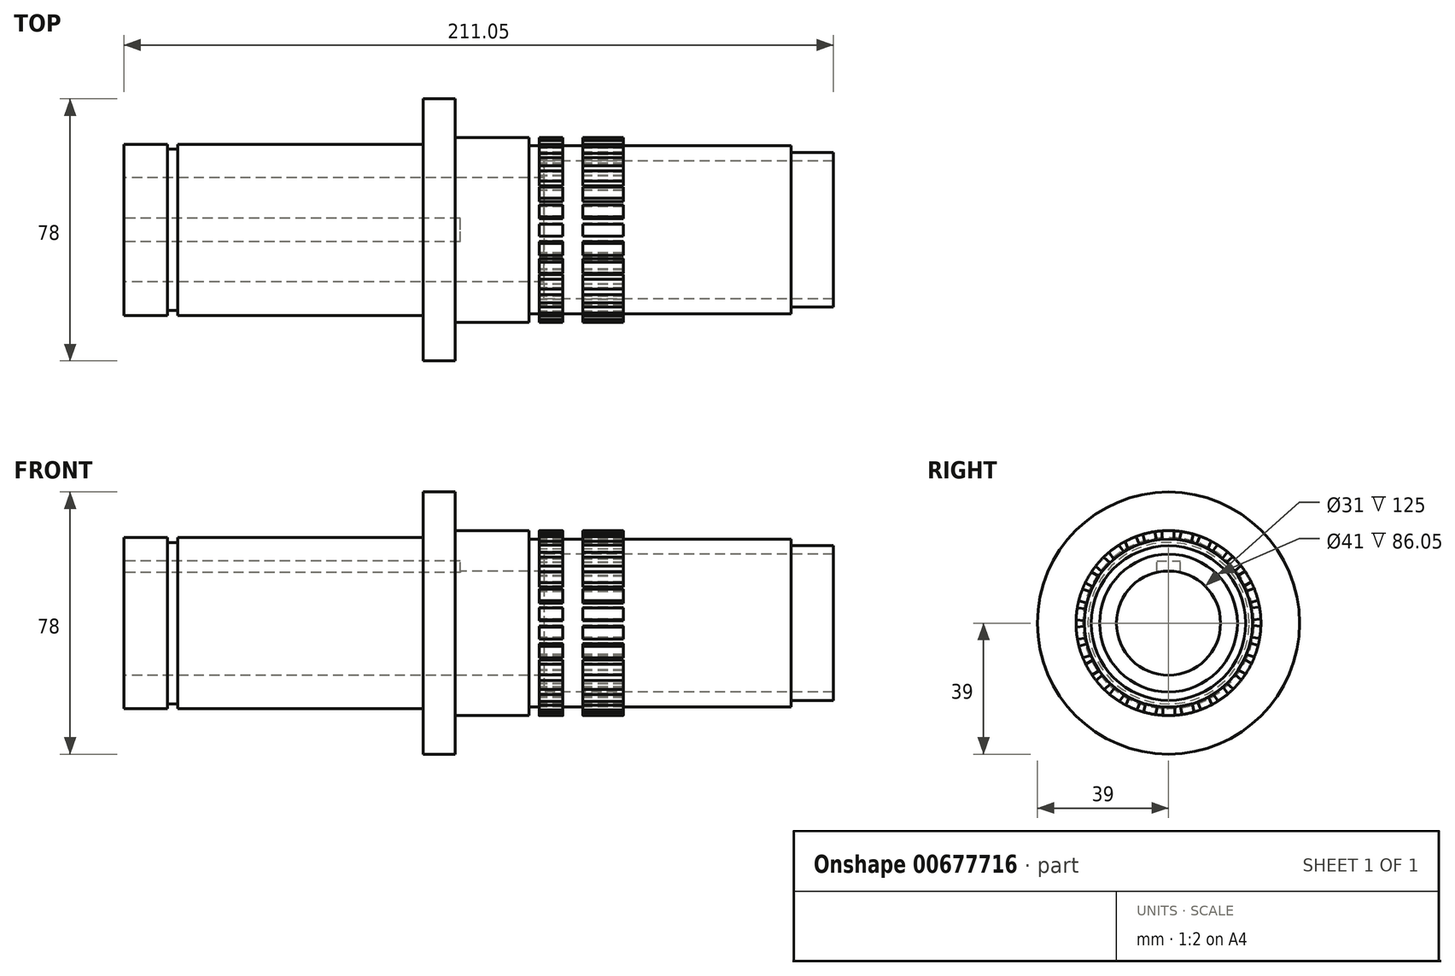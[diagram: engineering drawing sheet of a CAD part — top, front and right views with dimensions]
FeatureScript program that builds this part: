
annotation { "Feature Type Name" : "Feature", "Feature Type Description" : "" }
export const myFeature = defineFeature(function(context is Context, id is Id, definition is map)
    precondition{}
    {
        {
            var Q0;
            Q0=qCreatedBy(makeId("Front.planeOp"),FACE);
            var sketch = newSketch(context, id + "F0", { "sketchPlane" : qUnion([Q0])});
            skLineSegment(sketch, "E0", {"start": v(-135.23, 0) * mm, "end": v(176.63, 0) * mm, "construction": true});
            skLineSegment(sketch, "E1", {"start": v(-98.55, 15.5) * mm, "end": v(26.45, 15.5) * mm});
            skLineSegment(sketch, "E2", {"start": v(26.45, 15.5) * mm, "end": v(26.45, 20.5) * mm});
            skLineSegment(sketch, "E3", {"start": v(26.45, 20.5) * mm, "end": v(112.5, 20.5) * mm});
            skLineSegment(sketch, "E4", {"start": v(112.5, 20.5) * mm, "end": v(112.5, 23) * mm});
            skLineSegment(sketch, "E5", {"start": v(112.5, 23) * mm, "end": v(100, 23) * mm});
            skLineSegment(sketch, "E6", {"start": v(100, 23) * mm, "end": v(100, 25) * mm});
            skLineSegment(sketch, "E7", {"start": v(100, 25) * mm, "end": v(22, 25) * mm});
            skLineSegment(sketch, "E8", {"start": v(22, 25) * mm, "end": v(22, 27.5) * mm});
            skLineSegment(sketch, "E9", {"start": v(22, 27.5) * mm, "end": v(0, 27.5) * mm});
            skLineSegment(sketch, "E10", {"start": v(0, 27.5) * mm, "end": v(0, 39) * mm});
            skLineSegment(sketch, "E11", {"start": v(0, 39) * mm, "end": v(-9.55, 39) * mm});
            skLineSegment(sketch, "E12", {"start": v(-9.55, 39) * mm, "end": v(-9.55, 25.5) * mm});
            skLineSegment(sketch, "E13", {"start": v(-9.55, 25.5) * mm, "end": v(-82.55, 25.5) * mm});
            skLineSegment(sketch, "E14", {"start": v(-82.55, 25.5) * mm, "end": v(-82.55, 24) * mm});
            skLineSegment(sketch, "E15", {"start": v(-82.55, 24) * mm, "end": v(-85.55, 24) * mm});
            skLineSegment(sketch, "E16", {"start": v(-85.55, 24) * mm, "end": v(-85.55, 25.5) * mm});
            skLineSegment(sketch, "E17", {"start": v(-85.55, 25.5) * mm, "end": v(-98.55, 25.5) * mm});
            skLineSegment(sketch, "E18", {"start": v(-98.55, 25.5) * mm, "end": v(-98.55, 15.5) * mm});
            skSolve(sketch);
        }
        {
            var Q0;
            Q0=makeQuery(id+"F0.imprint","IMPRINT",FACE,{"disambiguationData":[TD([[makeQuery(id+"F0.imprint","IMPRINT",EDGE,{"derivedFrom":sQuery(id+"F0.wireOp",EDGE,"E1")}),1.0]])]});
            var Q1;
            Q1=sQuery(id+"F0.wireOp",EDGE,"E0");
            revolve(context, id + "F1", {"entities" : qUnion([Q0]), "axis" : qUnion([Q1]), "revolveType" : RevolveType.FULL});
        }
        {
            var Q0;
            Q0=makeQuery(id+"F1.opRevolve","SWEPT_FACE",FACE,{"disambiguationData":[OSD([sQuery(id+"F0.wireOp",EDGE,"E8")])]});
            cPlane(context, id + "F2", {"entities" : qUnion([Q0]), "cplaneType" : CPlaneType.OFFSET, "offset" : 3 * mm, "width" : 150 * mm, "height" : 150 * mm});
        }
        {
            var Q0;
            Q0=qCreatedBy(id+"F2.planeOp",FACE);
            var sketch = newSketch(context, id + "F3", { "sketchPlane" : qUnion([Q0])});
            skArc(sketch, "E19", {"start": v(1.7, 24.94) * mm, "mid": v(-0.11, 25) * mm, "end": v(-1.92, 24.93) * mm});
            skArc(sketch, "E20", {"start": v(1.7, 27.45) * mm, "mid": v(-0.11, 27.5) * mm, "end": v(-1.92, 27.43) * mm});
            skLineSegment(sketch, "E21", {"start": v(-1.92, 24.93) * mm, "end": v(-1.92, 27.43) * mm});
            skLineSegment(sketch, "E22", {"start": v(1.7, 27.45) * mm, "end": v(1.7, 24.94) * mm});
            skSolve(sketch);
        }
        {
            var Q0;
            Q0 = qSketchRegion(id + "F3", true);
            extrude(context, id + "F4", {"entities" : qUnion([Q0]), "depth" : 7 * mm, "offsetDistance" : 25 * mm});
        }
        {
            var Q0;
            Q0=makeQuery(id+"F4.opExtrude","CAP_FACE",FACE,{"disambiguationData":[OSD([sQuery(id+"F3.wireOp",EDGE,"E19"),sQuery(id+"F3.wireOp",EDGE,"E20"),sQuery(id+"F3.wireOp",EDGE,"E21"),sQuery(id+"F3.wireOp",EDGE,"E22")])],"isStart":false});
            cPlane(context, id + "F5", {"entities" : qUnion([Q0]), "cplaneType" : CPlaneType.OFFSET, "offset" : 6 * mm, "width" : 150 * mm, "height" : 150 * mm});
        }
        {
            var Q0;
            Q0=qCreatedBy(id+"F5.planeOp",FACE);
            var sketch = newSketch(context, id + "F6", { "sketchPlane" : qUnion([Q0])});
            skArc(sketch, "E23.0", {"start": v(1.7, 27.45) * mm, "mid": v(-0.11, 27.5) * mm, "end": v(-1.92, 27.43) * mm});
            skLineSegment(sketch, "E24.0", {"start": v(1.7, 27.45) * mm, "end": v(1.7, 24.94) * mm});
            skLineSegment(sketch, "E25.0", {"start": v(-1.92, 24.93) * mm, "end": v(-1.92, 27.43) * mm});
            skArc(sketch, "E26.0", {"start": v(1.7, 24.94) * mm, "mid": v(-0.11, 25) * mm, "end": v(-1.92, 24.93) * mm});
            skSolve(sketch);
        }
        {
            var Q0;
            Q0 = qSketchRegion(id + "F6", true);
            extrude(context, id + "F7", {"entities" : qUnion([Q0]), "depth" : 12 * mm, "offsetDistance" : 25 * mm});
        }
        {
            var Q0;
            Q0=makeQuery(id+"F1.opRevolve","SWEPT_FACE",FACE,{"disambiguationData":[OSD([sQuery(id+"F0.wireOp",EDGE,"E18")])]});
            var sketch = newSketch(context, id + "F8", { "sketchPlane" : qUnion([Q0])});
            skLineSegment(sketch, "E27.bottom", {"start": v(3.5, 12.5) * mm, "end": v(-3.5, 12.5) * mm});
            skLineSegment(sketch, "E27.top", {"start": v(3.5, 18.5) * mm, "end": v(-3.5, 18.5) * mm});
            skLineSegment(sketch, "E27.left", {"start": v(3.5, 12.5) * mm, "end": v(3.5, 18.5) * mm});
            skLineSegment(sketch, "E27.right", {"start": v(-3.5, 12.5) * mm, "end": v(-3.5, 18.5) * mm});
            skPoint(sketch, "E27.middle", {"position": v(0, 15.5) * mm});
            skSolve(sketch);
        }
        {
            var Q0;
            {var subQ0=sQuery(id+"F8.wireOp",EDGE,"E27.top");Q0=makeQuery(id+"F8.imprint","IMPRINT",FACE,{"disambiguationData":[TD([[makeQuery(id+"F8.imprint","IMPRINT",EDGE,{"derivedFrom":subQ0}),1.0]])]});}
            extrude(context, id + "F9", {"entities" : qUnion([Q0]), "operationType" : NewBodyOperationType.REMOVE, "oppositeDirection" : true, "depth" : 100 * mm, "offsetDistance" : 25 * mm});
        }
        {
            var Q0;
            Q0=makeQuery(id+"F7.opExtrude","SWEPT_BODY",BODY,{"disambiguationData":[OSD([sQuery(id+"F6.wireOp",EDGE,"E23.0"),sQuery(id+"F6.wireOp",EDGE,"E24.0"),sQuery(id+"F6.wireOp",EDGE,"E25.0"),sQuery(id+"F6.wireOp",EDGE,"E26.0")])]});
            var Q1;
            Q1=makeQuery(id+"F1.opRevolve","SWEPT_FACE",FACE,{"disambiguationData":[OSD([sQuery(id+"F0.wireOp",EDGE,"E11")])]});
            circularPattern(context, id + "F10", {"entities" : qUnion([Q0]), "axis" : qUnion([Q1]), "angle" : 360 * degree, "instanceCount" : 30, "equalSpace" : true});
        }
        {
            var Q0;
            Q0=makeQuery(id+"F4.opExtrude","SWEPT_BODY",BODY,{"disambiguationData":[OSD([sQuery(id+"F3.wireOp",EDGE,"E19"),sQuery(id+"F3.wireOp",EDGE,"E20"),sQuery(id+"F3.wireOp",EDGE,"E21"),sQuery(id+"F3.wireOp",EDGE,"E22")])]});
            var Q1;
            Q1=makeQuery(id+"F1.opRevolve","SWEPT_FACE",FACE,{"disambiguationData":[OSD([sQuery(id+"F0.wireOp",EDGE,"E11")])]});
            circularPattern(context, id + "F11", {"entities" : qUnion([Q0]), "axis" : qUnion([Q1]), "angle" : 360 * degree, "instanceCount" : 30, "equalSpace" : true});
        }
    });
